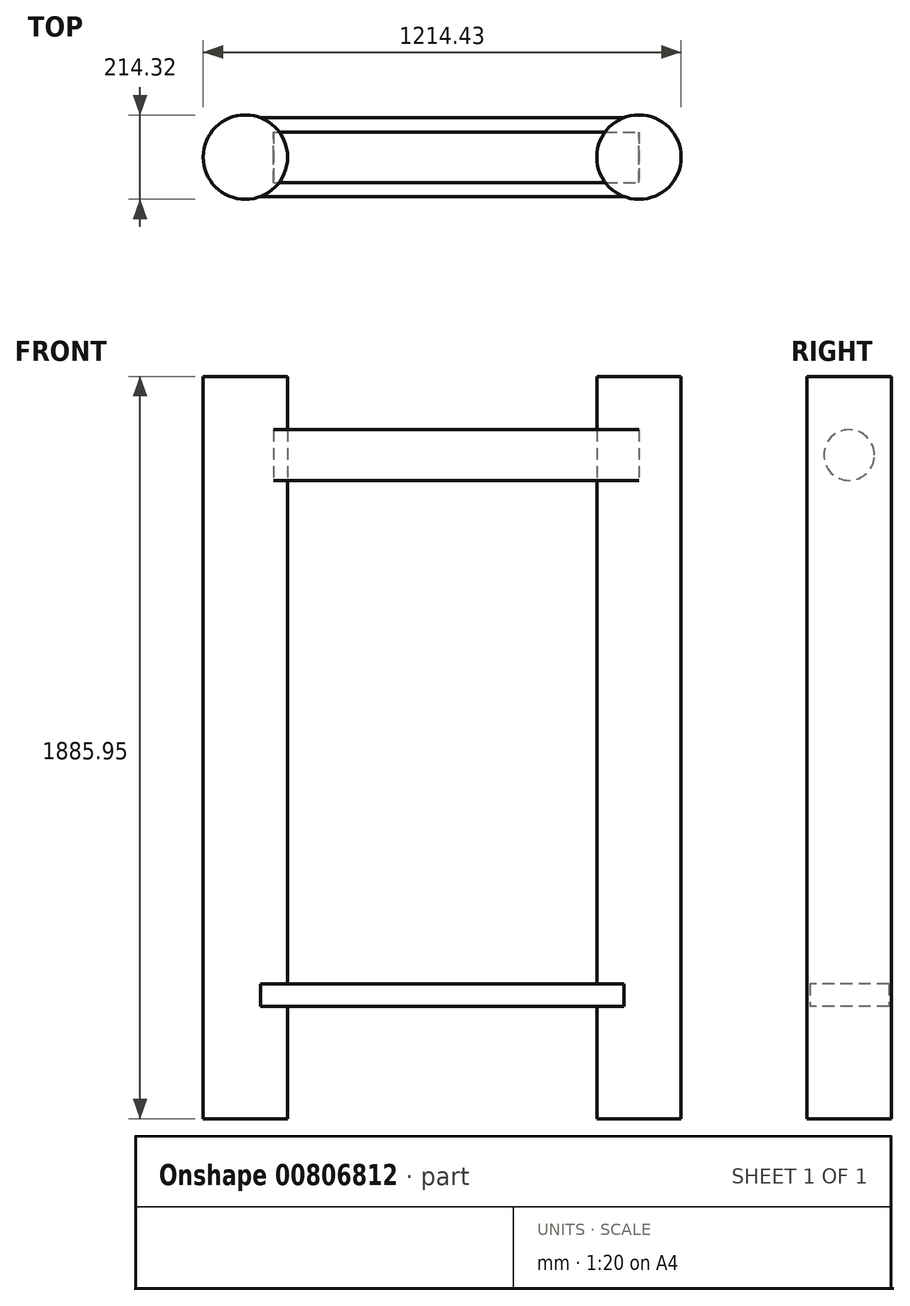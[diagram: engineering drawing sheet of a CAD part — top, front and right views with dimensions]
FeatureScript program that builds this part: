
annotation { "Feature Type Name" : "Feature", "Feature Type Description" : "" }
export const myFeature = defineFeature(function(context is Context, id is Id, definition is map)
    precondition{}
    {
        {
            var Q0;
            Q0=qCreatedBy(makeId("Top.planeOp"),FACE);
            var sketch = newSketch(context, id + "F0", { "sketchPlane" : qUnion([Q0])});
            skLineSegment(sketch, "E0.bottom", {"start": v(-191.26, 0) * mm, "end": v(164.34, 0) * mm});
            skLineSegment(sketch, "E0.top", {"start": v(-191.26, 1778) * mm, "end": v(164.34, 1778) * mm});
            skLineSegment(sketch, "E0.left", {"start": v(-191.26, 0) * mm, "end": v(-191.26, 1778) * mm});
            skLineSegment(sketch, "E0.right", {"start": v(164.34, 0) * mm, "end": v(164.34, 1778) * mm});
            skPoint(sketch, "E1", {"position": v(0, 1778) * mm});
            skSolve(sketch);
        }
        {
            var Q0;
            Q0=makeQuery(id+"F0.imprint","IMPRINT",FACE,{"disambiguationData":[TD([[makeQuery(id+"F0.imprint","IMPRINT",EDGE,{"derivedFrom":sQuery(id+"F0.wireOp",EDGE,"E0.bottom")}),1.0]])]});
            extrude(context, id + "F1", {"entities" : qUnion([Q0]), "depth" : 50.8 * mm, "offsetDistance" : 25.4 * mm, "hasSecondDirection" : true, "secondDirectionOppositeDirection" : true, "secondDirectionDepth" : 50.8 * mm});
        }
        {
            var Q0;
            Q0=makeQuery(id+"F1.opExtrude","CAP_FACE",FACE,{"disambiguationData":[OSD([sQuery(id+"F0.wireOp",EDGE,"E0.bottom"),sQuery(id+"F0.wireOp",EDGE,"E0.top"),sQuery(id+"F0.wireOp",EDGE,"E0.left"),sQuery(id+"F0.wireOp",EDGE,"E0.right")])],"isStart":false});
            var sketch = newSketch(context, id + "F2", { "sketchPlane" : qUnion([Q0])});
            skCircle(sketch, "E2", {"center": v(-13.46, 1778) * mm, "radius": 190.5 * mm});
            skSolve(sketch);
        }
        {
            var Q0;
            {var subQ5=makeQuery(id+"F1.opExtrude","CAP_EDGE",EDGE,{"disambiguationData":[OSD([sQuery(id+"F0.wireOp",EDGE,"E0.top")])],"isStart":false});Q0=makeQuery(id+"F2.imprint","IMPRINT",FACE,{"disambiguationData":[TD([[makeQuery(id+"F2.imprint","IMPRINT",EDGE,{"derivedFrom":subQ5}),1.0]])]});}
            var Q1;
            {var subQ5=makeQuery(id+"F1.opExtrude","CAP_EDGE",EDGE,{"disambiguationData":[OSD([sQuery(id+"F0.wireOp",EDGE,"E0.top")])],"isStart":false});Q1=makeQuery(id+"F2.imprint","IMPRINT",FACE,{"disambiguationData":[TD([[makeQuery(id+"F2.imprint","IMPRINT",EDGE,{"derivedFrom":subQ5}),-1.0]])]});}
            extrude(context, id + "F3", {"entities" : qUnion([Q0, Q1]), "operationType" : NewBodyOperationType.ADD, "depth" : 2743.2 * mm, "offsetDistance" : 25.4 * mm, "hasSecondDirection" : true, "secondDirectionOppositeDirection" : true, "secondDirectionDepth" : 609.6 * mm});
        }
        {
            var Q0;
            Q0=makeQuery(id+"F1.opExtrude","CAP_FACE",FACE,{"disambiguationData":[OSD([sQuery(id+"F0.wireOp",EDGE,"E0.bottom"),sQuery(id+"F0.wireOp",EDGE,"E0.top"),sQuery(id+"F0.wireOp",EDGE,"E0.left"),sQuery(id+"F0.wireOp",EDGE,"E0.right")])],"isStart":false});
            var sketch = newSketch(context, id + "F4", { "sketchPlane" : qUnion([Q0])});
            skPoint(sketch, "E3", {"position": v(-13.46, 0) * mm});
            skSolve(sketch);
        }
        {
            var Q0;
            {var subQ0=sQuery(id+"F0.wireOp",EDGE,"E0.bottom");Q0=makeQuery(id+"F4.imprint","IMPRINT",FACE,{"disambiguationData":[TD([[makeQuery(id+"F4.imprint","IMPRINT",EDGE,{"derivedFrom":makeQuery(id+"F1.opExtrude","CAP_EDGE",EDGE,{"disambiguationData":[OSD([subQ0])],"isStart":false})}),1.0]])]});}
            var sketch = newSketch(context, id + "F5", { "sketchPlane" : qUnion([Q0])});
            skCircle(sketch, "E4", {"center": v(-13.47, 0) * mm, "radius": 190.5 * mm});
            skSolve(sketch);
        }
        {
            var Q0;
            {var subQ5=makeQuery(id+"F4.imprint","IMPRINT",EDGE,{"derivedFrom":makeQuery(id+"F1.opExtrude","CAP_EDGE",EDGE,{"disambiguationData":[OSD([sQuery(id+"F0.wireOp",EDGE,"E0.bottom")])],"isStart":false})});Q0=makeQuery(id+"F5.imprint","IMPRINT",FACE,{"disambiguationData":[TD([[makeQuery(id+"F5.imprint","IMPRINT",EDGE,{"derivedFrom":subQ5}),-1.0]])]});}
            var Q1;
            {var subQ5=makeQuery(id+"F4.imprint","IMPRINT",EDGE,{"derivedFrom":makeQuery(id+"F1.opExtrude","CAP_EDGE",EDGE,{"disambiguationData":[OSD([sQuery(id+"F0.wireOp",EDGE,"E0.bottom")])],"isStart":false})});Q1=makeQuery(id+"F5.imprint","IMPRINT",FACE,{"disambiguationData":[TD([[makeQuery(id+"F5.imprint","IMPRINT",EDGE,{"derivedFrom":subQ5}),1.0]])]});}
            extrude(context, id + "F6", {"entities" : qUnion([Q0, Q1]), "operationType" : NewBodyOperationType.ADD, "depth" : 2743.2 * mm, "offsetDistance" : 25.4 * mm, "hasSecondDirection" : true, "secondDirectionOppositeDirection" : true, "secondDirectionDepth" : 609.6 * mm});
        }
        {
            var Q0;
            Q0=qCreatedBy(makeId("Right.planeOp"),FACE);
            var sketch = newSketch(context, id + "F7", { "sketchPlane" : qUnion([Q0])});
            skLineSegment(sketch, "E5", {"start": v(0, 0) * mm, "end": v(0, 2438.4) * mm});
            skLineSegment(sketch, "E6", {"start": v(0, 2438.4) * mm, "end": v(1777.2, 2438.4) * mm});
            skSolve(sketch);
        }
        {
            var Q0;
            Q0=sQuery(id+"F7.wireOp",VERTEX,"E5.end");
            var Q1;
            Q1=sQuery(id+"F7.wireOp",EDGE,"E6");
            cPlane(context, id + "F8", {"entities" : qUnion([Q0, Q1]), "cplaneType" : CPlaneType.LINE_POINT, "offset" : 25.4 * mm, "width" : 152.4 * mm, "height" : 152.4 * mm});
        }
        {
            var Q0;
            Q0=qCreatedBy(id+"F8.planeOp",FACE);
            var sketch = newSketch(context, id + "F9", { "sketchPlane" : qUnion([Q0])});
            skCircle(sketch, "E7", {"center": v(14.64, 2438.69) * mm, "radius": 114.3 * mm});
            skSolve(sketch);
        }
        {
            var Q0;
            Q0=makeQuery(id+"F9.imprint","IMPRINT",FACE,{"disambiguationData":[TD([[makeQuery(id+"F9.imprint","IMPRINT",EDGE,{"derivedFrom":sQuery(id+"F9.wireOp",EDGE,"E7")}),1.0]])]});
            var Q1;
            Q1=sQuery(id+"F9.wireOp",EDGE,"E7");
            extrude(context, id + "F10", {"entities" : qUnion([Q0]), "surfaceEntities" : qUnion([Q1]), "depth" : 1651 * mm, "offsetDistance" : 25.4 * mm});
        }
        {
            var Q0;
            Q0=makeQuery(id+"F10.opExtrude","SWEPT_BODY",BODY,{"disambiguationData":[OSD([sQuery(id+"F9.wireOp",EDGE,"E7")])]});
            var Q1;
            Q1=makeQuery(id+"F1.opExtrude","SWEPT_BODY",BODY,{"disambiguationData":[OSD([sQuery(id+"F0.wireOp",EDGE,"E0.bottom"),sQuery(id+"F0.wireOp",EDGE,"E0.top"),sQuery(id+"F0.wireOp",EDGE,"E0.left"),sQuery(id+"F0.wireOp",EDGE,"E0.right")])]});
            var Q2;
            Q2=makeQuery(id+"F1.opExtrude","CAP_EDGE",EDGE,{"disambiguationData":[OSD([sQuery(id+"F0.wireOp",EDGE,"E0.right")])],"isStart":false});
            var Q3;
            Q3=sQuery(id+"F7.wireOp",EDGE,"E5");
            transform(context, id + "F11", {"entities" : qUnion([Q0, Q1]), "transformType" : TransformType.ROTATION, "transformAxis" : qUnion([Q3]), "angle" : 90 * degree, "makeCopy" : false});
        }
        {
            var Q0;
            Q0=makeQuery(id+"F10.opExtrude","SWEPT_BODY",BODY,{"disambiguationData":[OSD([sQuery(id+"F9.wireOp",EDGE,"E7")])]});
            var Q1;
            Q1=makeQuery(id+"F1.opExtrude","SWEPT_BODY",BODY,{"disambiguationData":[OSD([sQuery(id+"F0.wireOp",EDGE,"E0.bottom"),sQuery(id+"F0.wireOp",EDGE,"E0.top"),sQuery(id+"F0.wireOp",EDGE,"E0.left"),sQuery(id+"F0.wireOp",EDGE,"E0.right")])]});
            var Q2;
            Q2=sQuery(id+"F4.wireOp",VERTEX,"E3");
            transform(context, id + "F12", {"entities" : qUnion([Q0, Q1]), "transformType" : TransformType.SCALE_UNIFORMLY, "scale" : .75, "scalePoint" : qUnion([Q2]), "makeCopy" : false});
        }
        {
            var Q0;
            Q0=makeQuery(id+"F1.opExtrude","SWEPT_BODY",BODY,{"disambiguationData":[OSD([sQuery(id+"F0.wireOp",EDGE,"E0.bottom"),sQuery(id+"F0.wireOp",EDGE,"E0.top"),sQuery(id+"F0.wireOp",EDGE,"E0.left"),sQuery(id+"F0.wireOp",EDGE,"E0.right")])]});
            var Q1;
            Q1=makeQuery(id+"F10.opExtrude","SWEPT_BODY",BODY,{"disambiguationData":[OSD([sQuery(id+"F9.wireOp",EDGE,"E7")])]});
            var Q2;
            Q2=qCreatedBy(makeId("Origin.pointOp"),VERTEX);
            transform(context, id + "F13", {"entities" : qUnion([Q0, Q1]), "transformType" : TransformType.SCALE_UNIFORMLY, "scale" : .75, "scalePoint" : qUnion([Q2]), "makeCopy" : false});
        }
    });
